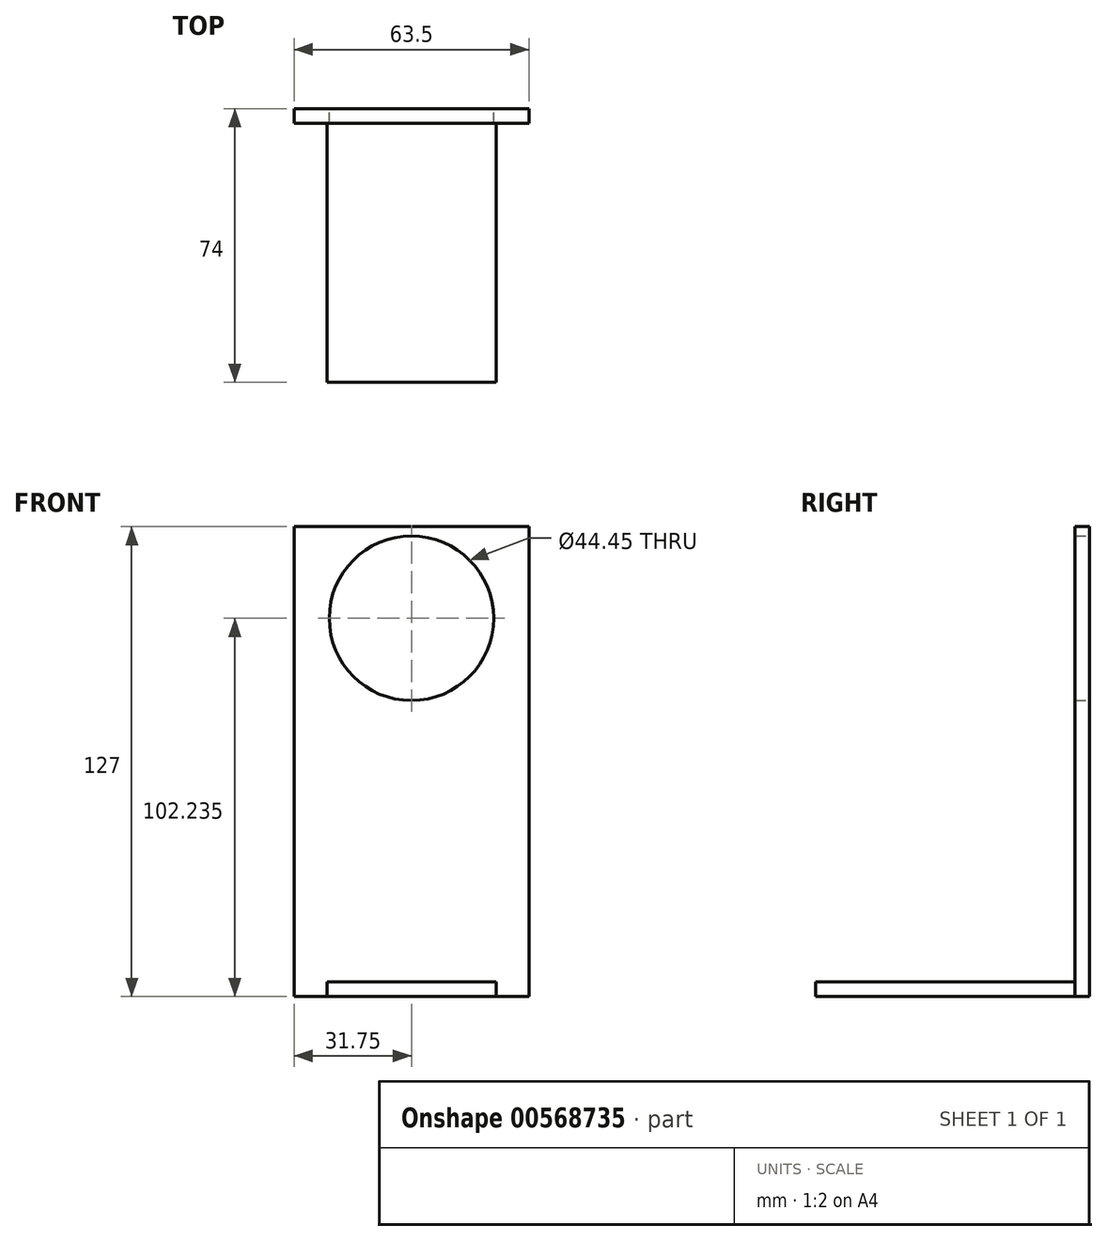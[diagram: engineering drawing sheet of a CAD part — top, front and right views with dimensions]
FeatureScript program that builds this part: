
annotation { "Feature Type Name" : "Feature", "Feature Type Description" : "" }
export const myFeature = defineFeature(function(context is Context, id is Id, definition is map)
    precondition{}
    {
        {
            var Q0;
            Q0=qCreatedBy(makeId("Front.planeOp"),FACE);
            var sketch = newSketch(context, id + "F0", { "sketchPlane" : qUnion([Q0])});
            skLineSegment(sketch, "E0.bottom", {"start": v(0, 0) * mm, "end": v(63.5, 0) * mm});
            skLineSegment(sketch, "E0.top", {"start": v(0, 127) * mm, "end": v(63.5, 127) * mm});
            skLineSegment(sketch, "E0.left", {"start": v(0, 0) * mm, "end": v(0, 127) * mm});
            skLineSegment(sketch, "E0.right", {"start": v(63.5, 0) * mm, "end": v(63.5, 127) * mm});
            skCircle(sketch, "E1", {"center": v(31.75, 102.23) * mm, "radius": 22.23 * mm});
            skSolve(sketch);
        }
        {
            var Q0;
            Q0 = qSketchRegion(id + "F0", true);
            extrude(context, id + "F1", {"entities" : qUnion([Q0]), "depth" : 4 * mm, "offsetDistance" : 25.4 * mm});
        }
        {
            var Q0;
            Q0=makeQuery(id+"F1.opExtrude","CAP_FACE",FACE,{"disambiguationData":[OSD([sQuery(id+"F0.wireOp",EDGE,"E0.bottom"),sQuery(id+"F0.wireOp",EDGE,"E0.top"),sQuery(id+"F0.wireOp",EDGE,"E0.left"),sQuery(id+"F0.wireOp",EDGE,"E0.right"),sQuery(id+"F0.wireOp",EDGE,"E1")])],"isStart":false});
            var sketch = newSketch(context, id + "F2", { "sketchPlane" : qUnion([Q0])});
            skLineSegment(sketch, "E2", {"start": v(0, 4) * mm, "end": v(63.5, 4) * mm});
            skLineSegment(sketch, "E3", {"start": v(63.5, 0) * mm, "end": v(0, 0) * mm});
            skLineSegment(sketch, "E4", {"start": v(8.9, 4) * mm, "end": v(8.9, 0) * mm});
            skLineSegment(sketch, "E5", {"start": v(54.6, 4) * mm, "end": v(54.6, 0) * mm});
            skSolve(sketch);
        }
        {
            var Q0;
            Q0 = qSketchRegion(id + "F2", true);
            extrude(context, id + "F3", {"entities" : qUnion([Q0]), "operationType" : NewBodyOperationType.ADD, "depth" : 70 * mm, "offsetDistance" : 25.4 * mm});
        }
    });
